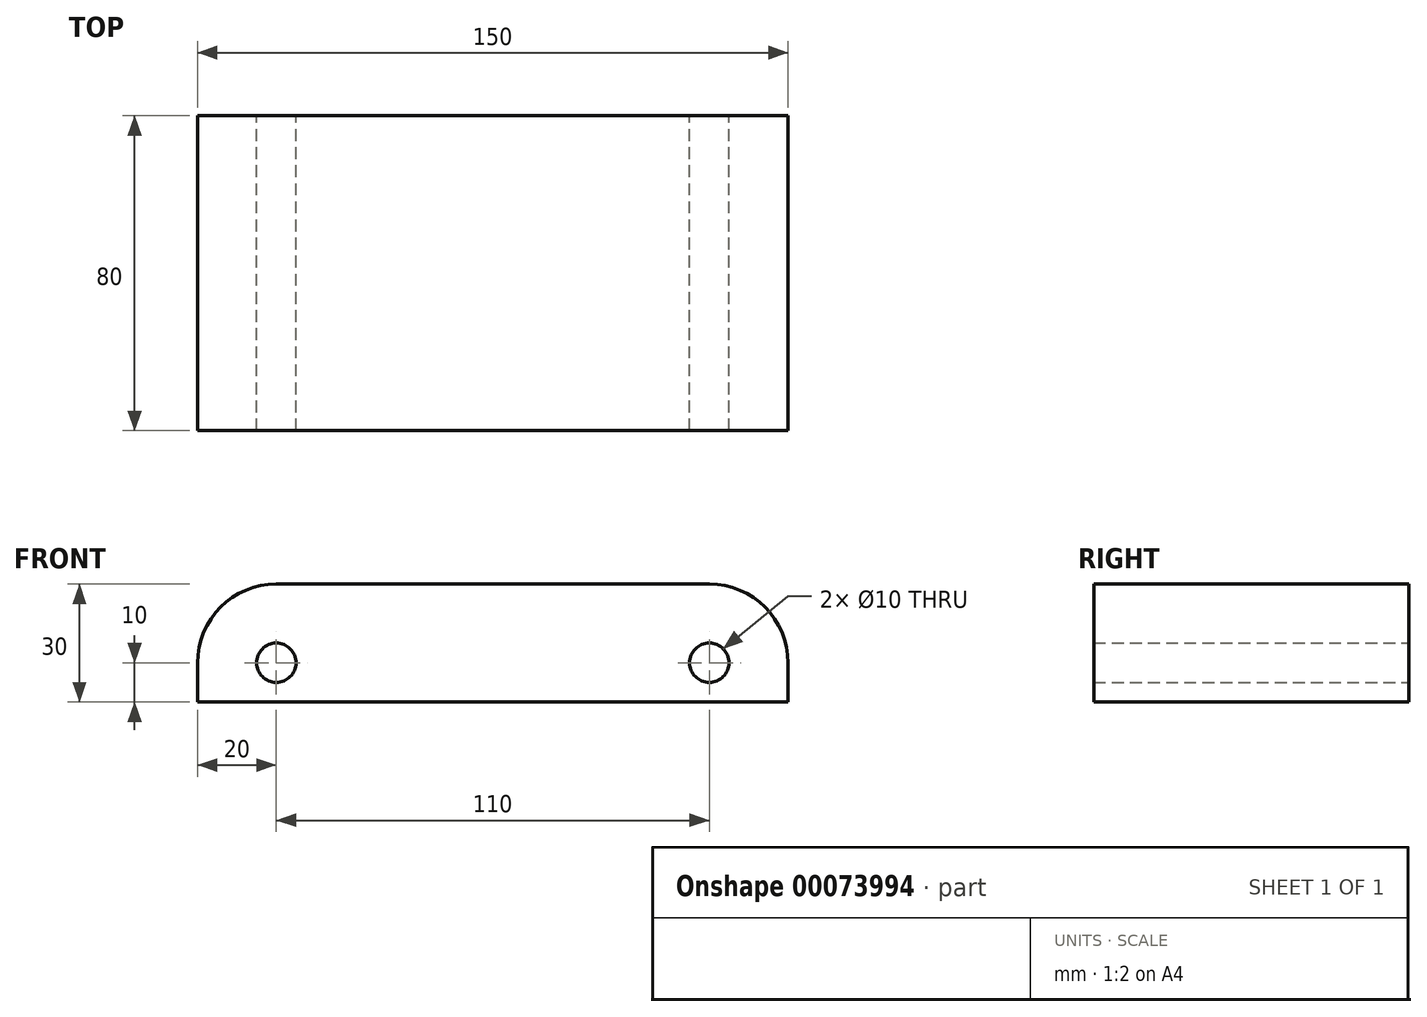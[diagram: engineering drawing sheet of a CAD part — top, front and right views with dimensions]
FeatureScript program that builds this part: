
annotation { "Feature Type Name" : "Feature", "Feature Type Description" : "" }
export const myFeature = defineFeature(function(context is Context, id is Id, definition is map)
    precondition{}
    {
        {
            var Q0;
            Q0=qCreatedBy(makeId("Front.planeOp"),FACE);
            var sketch = newSketch(context, id + "F0", { "sketchPlane" : qUnion([Q0])});
            skLineSegment(sketch, "E0.bottom", {"start": v(0, 0) * mm, "end": v(150, 0) * mm});
            skLineSegment(sketch, "E0.top", {"start": v(20, 30) * mm, "end": v(130, 30) * mm});
            skLineSegment(sketch, "E0.left", {"start": v(0, 0) * mm, "end": v(0, 10) * mm});
            skLineSegment(sketch, "E0.right", {"start": v(150, 0) * mm, "end": v(150, 10) * mm});
            skPoint(sketch, "E1.visualSharp", {"position": v(0, 30) * mm});
            skArc(sketch, "E1.filletArc", {"start": v(20, 30) * mm, "mid": v(5.86, 24.14) * mm, "end": v(0, 10) * mm});
            skPoint(sketch, "E2.visualSharp", {"position": v(150, 30) * mm});
            skArc(sketch, "E2.filletArc", {"start": v(150, 10) * mm, "mid": v(144.14, 24.14) * mm, "end": v(130, 30) * mm});
            skCircle(sketch, "E3", {"center": v(20, 10) * mm, "radius": 5 * mm});
            skCircle(sketch, "E4", {"center": v(130, 10) * mm, "radius": 5 * mm});
            skSolve(sketch);
        }
        {
            var Q0;
            Q0=makeQuery(id+"F0.imprint","IMPRINT",FACE,{"disambiguationData":[TD([[makeQuery(id+"F0.imprint","IMPRINT",EDGE,{"derivedFrom":sQuery(id+"F0.wireOp",EDGE,"E0.bottom")}),1.0]])]});
            extrude(context, id + "F1", {"entities" : qUnion([Q0]), "depth" : 80 * mm});
        }
    });
